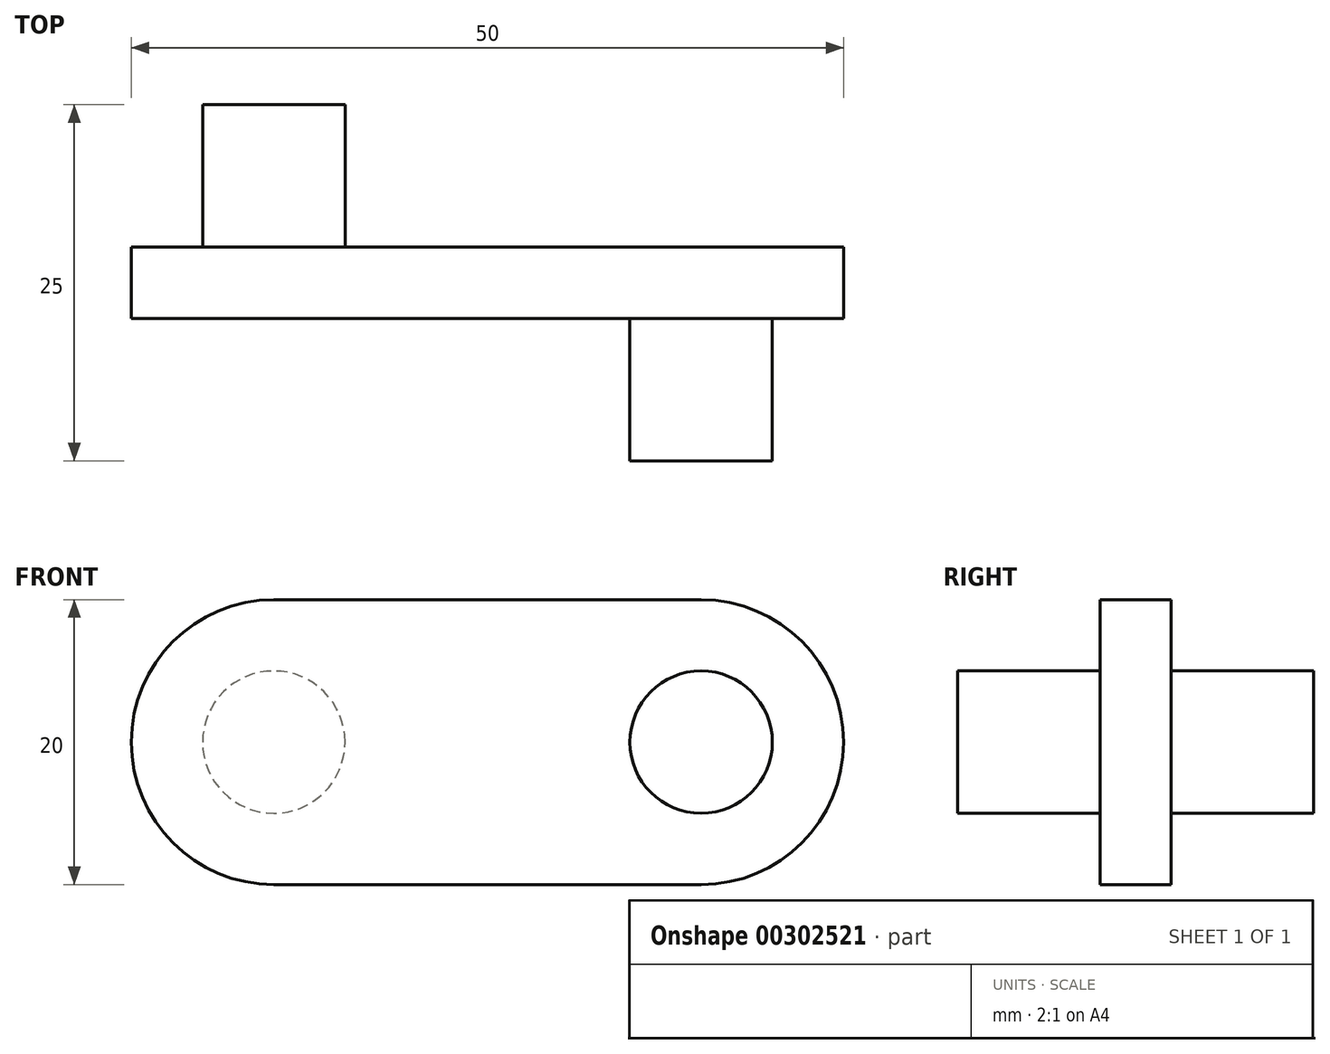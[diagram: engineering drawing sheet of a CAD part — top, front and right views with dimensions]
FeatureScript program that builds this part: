
annotation { "Feature Type Name" : "Feature", "Feature Type Description" : "" }
export const myFeature = defineFeature(function(context is Context, id is Id, definition is map)
    precondition{}
    {
        {
            var Q0;
            Q0=qCreatedBy(makeId("Front.planeOp"),FACE);
            var sketch = newSketch(context, id + "F0", { "sketchPlane" : qUnion([Q0])});
            skArc(sketch, "E0", {"start": v(0, 10) * mm, "mid": v(-10, 0) * mm, "end": v(0, -10) * mm});
            skArc(sketch, "E1", {"start": v(30, -10) * mm, "mid": v(40, 0) * mm, "end": v(30, 10) * mm});
            skLineSegment(sketch, "E2", {"start": v(0, 10) * mm, "end": v(30, 10) * mm});
            skLineSegment(sketch, "E3", {"start": v(0, -10) * mm, "end": v(30, -10) * mm});
            skSolve(sketch);
        }
        {
            var Q0;
            Q0=makeQuery(id+"F0.imprint","IMPRINT",FACE,{"disambiguationData":[TD([[makeQuery(id+"F0.imprint","IMPRINT",EDGE,{"derivedFrom":sQuery(id+"F0.wireOp",EDGE,"E0")}),1.0]])]});
            extrude(context, id + "F1", {"entities" : qUnion([Q0]), "depth" : 5 * mm});
        }
        {
            var Q0;
            Q0=makeQuery(id+"F1.opExtrude","CAP_FACE",FACE,{"disambiguationData":[OSD([sQuery(id+"F0.wireOp",EDGE,"E0"),sQuery(id+"F0.wireOp",EDGE,"E1"),sQuery(id+"F0.wireOp",EDGE,"E2"),sQuery(id+"F0.wireOp",EDGE,"E3")])],"isStart":false});
            var sketch = newSketch(context, id + "F2", { "sketchPlane" : qUnion([Q0])});
            skArc(sketch, "E4.0", {"start": v(30, -10) * mm, "mid": v(40, 0) * mm, "end": v(30, 10) * mm});
            skCircle(sketch, "E5", {"center": v(30, 0) * mm, "radius": 5 * mm});
            skSolve(sketch);
        }
        {
            var Q0;
            Q0=makeQuery(id+"F2.imprint","IMPRINT",FACE,{"disambiguationData":[TD([[makeQuery(id+"F2.imprint","IMPRINT",EDGE,{"derivedFrom":sQuery(id+"F2.wireOp",EDGE,"E5")}),1.0]])]});
            extrude(context, id + "F3", {"entities" : qUnion([Q0]), "operationType" : NewBodyOperationType.ADD, "depth" : 10 * mm});
        }
        {
            var Q0;
            Q0=makeQuery(id+"F1.opExtrude","CAP_FACE",FACE,{"disambiguationData":[OSD([sQuery(id+"F0.wireOp",EDGE,"E0"),sQuery(id+"F0.wireOp",EDGE,"E1"),sQuery(id+"F0.wireOp",EDGE,"E2"),sQuery(id+"F0.wireOp",EDGE,"E3")])],"isStart":true});
            var sketch = newSketch(context, id + "F4", { "sketchPlane" : qUnion([Q0])});
            skCircle(sketch, "E6", {"center": v(0, 0) * mm, "radius": 5 * mm});
            skSolve(sketch);
        }
        {
            var Q0;
            Q0=makeQuery(id+"F4.imprint","IMPRINT",FACE,{"disambiguationData":[TD([[makeQuery(id+"F4.imprint","IMPRINT",EDGE,{"derivedFrom":sQuery(id+"F4.wireOp",EDGE,"E6")}),1.0]])]});
            extrude(context, id + "F5", {"entities" : qUnion([Q0]), "operationType" : NewBodyOperationType.ADD, "depth" : 10 * mm});
        }
    });
